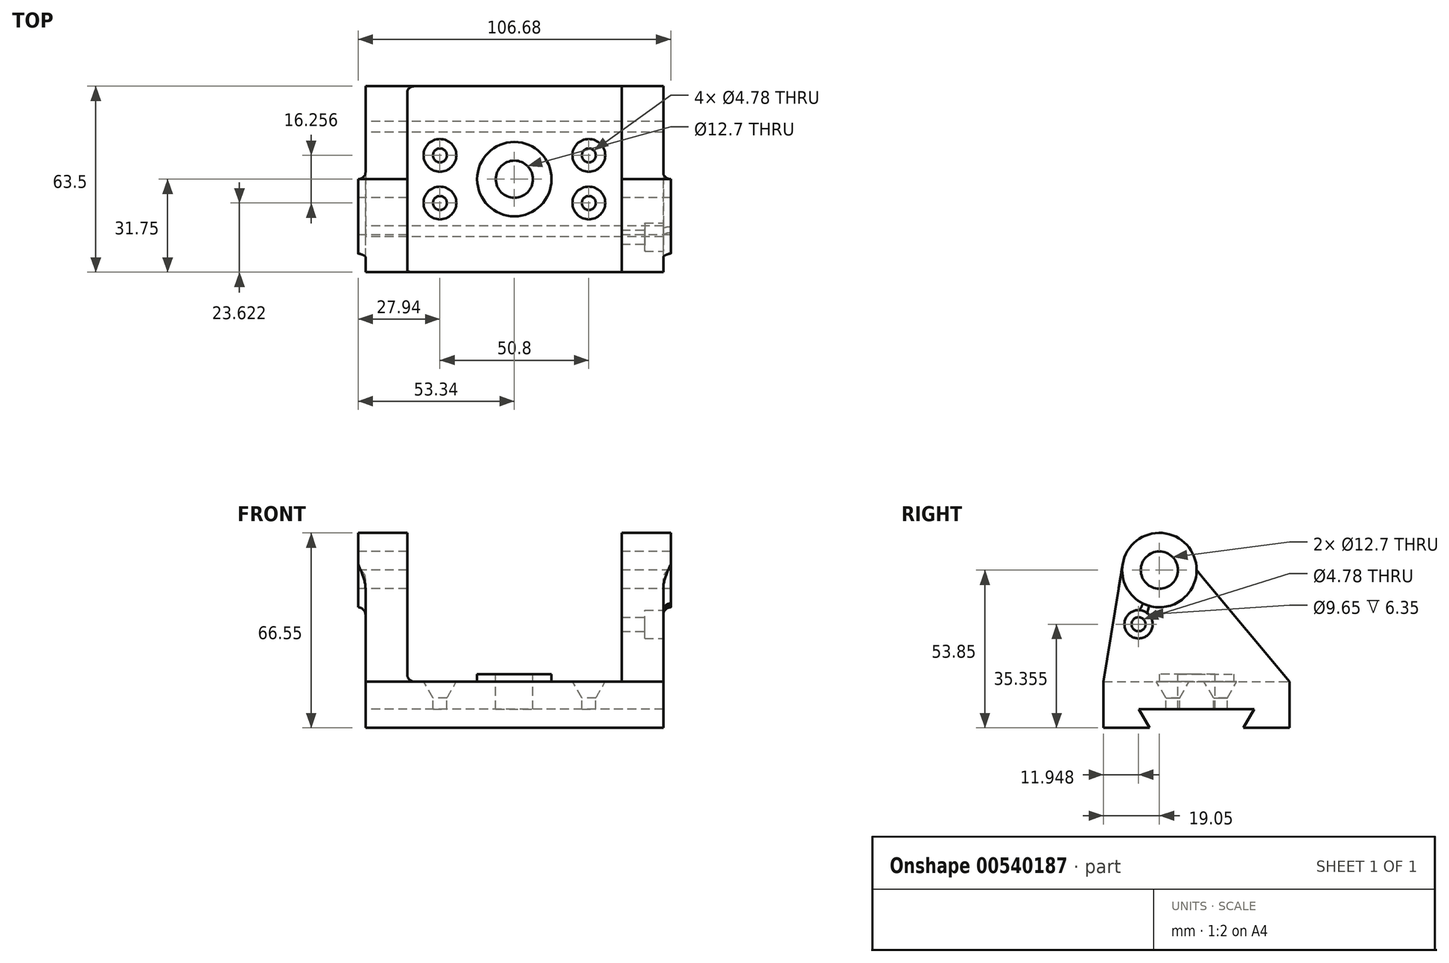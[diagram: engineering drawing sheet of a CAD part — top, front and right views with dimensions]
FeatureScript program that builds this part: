
annotation { "Feature Type Name" : "Feature", "Feature Type Description" : "" }
export const myFeature = defineFeature(function(context is Context, id is Id, definition is map)
    precondition{}
    {
        {
            var Q0;
            Q0=qCreatedBy(makeId("Right.planeOp"),FACE);
            var sketch = newSketch(context, id + "F0", { "sketchPlane" : qUnion([Q0])});
            skLineSegment(sketch, "E0", {"start": v(0, -77.1) * mm, "end": v(0, 79.46) * mm, "construction": true});
            skLineSegment(sketch, "E1", {"start": v(-83.92, 0) * mm, "end": v(89.2, 0) * mm, "construction": true});
            skLineSegment(sketch, "E2", {"start": v(-31.75, 0) * mm, "end": v(-31.75, -15.75) * mm});
            skLineSegment(sketch, "E3", {"start": v(-31.75, -15.75) * mm, "end": v(-16, -15.75) * mm});
            skCircle(sketch, "E4", {"center": v(-12.7, 38.1) * mm, "radius": 12.7 * mm});
            skCircle(sketch, "E5", {"center": v(-12.7, 38.1) * mm, "radius": 6.35 * mm});
            skLineSegment(sketch, "E6", {"start": v(-31.75, 0) * mm, "end": v(-25.24, 40.13) * mm});
            skLineSegment(sketch, "E7", {"start": v(0, -9.4) * mm, "end": v(-19.67, -9.4) * mm});
            skLineSegment(sketch, "E8", {"start": v(-19.67, -9.4) * mm, "end": v(-16, -15.75) * mm});
            skLineSegment(sketch, "E9.MirrorCS", {"start": v(0, -9.4) * mm, "end": v(19.67, -9.4) * mm});
            skLineSegment(sketch, "E10.MirrorCS", {"start": v(19.67, -9.4) * mm, "end": v(16, -15.75) * mm});
            skLineSegment(sketch, "E11.MirrorCS", {"start": v(31.75, -15.75) * mm, "end": v(16, -15.75) * mm});
            skLineSegment(sketch, "E12.MirrorCS", {"start": v(31.75, 0) * mm, "end": v(31.75, -15.75) * mm});
            skLineSegment(sketch, "E13", {"start": v(31.75, 0) * mm, "end": v(0, 38.1) * mm});
            skLineSegment(sketch, "E14", {"start": v(-31.75, 0) * mm, "end": v(31.75, 0) * mm});
            skSolve(sketch);
        }
        {
            var Q0;
            Q0=makeQuery(id+"F0.imprint","IMPRINT",FACE,{"disambiguationData":[TD([[makeQuery(id+"F0.imprint","IMPRINT",EDGE,{"derivedFrom":sQuery(id+"F0.wireOp",EDGE,"E2")}),1.0]])]});
            var Q1;
            Q1=makeQuery(id+"F0.imprint","IMPRINT",FACE,{"disambiguationData":[TD([[makeQuery(id+"F0.imprint","IMPRINT",EDGE,{"derivedFrom":sQuery(id+"F0.wireOp",EDGE,"E5")}),-1.0]])]});
            var Q2;
            {var subQ0=sQuery(id+"F0.wireOp",EDGE,"E6");Q2=makeQuery(id+"F0.imprint","IMPRINT",FACE,{"disambiguationData":[TD([[makeQuery(id+"F0.imprint","IMPRINT",EDGE,{"derivedFrom":subQ0}),-1.0]])]});}
            extrude(context, id + "F1", {"entities" : qUnion([Q0, Q1, Q2]), "endBound" : BoundingType.SYMMETRIC, "depth" : 101.6 * mm, "offsetDistance" : 25.4 * mm});
        }
        {
            var Q0;
            Q0=makeQuery(id+"F0.imprint","IMPRINT",FACE,{"disambiguationData":[TD([[makeQuery(id+"F0.imprint","IMPRINT",EDGE,{"derivedFrom":sQuery(id+"F0.wireOp",EDGE,"E5")}),-1.0]])]});
            extrude(context, id + "F2", {"entities" : qUnion([Q0]), "operationType" : NewBodyOperationType.ADD, "endBound" : BoundingType.SYMMETRIC, "depth" : 106.68 * mm, "offsetDistance" : 25.4 * mm});
        }
        {
            var Q0;
            {var subQ0=sQuery(id+"F0.wireOp",EDGE,"E6");Q0=makeQuery(id+"F0.imprint","IMPRINT",FACE,{"disambiguationData":[TD([[makeQuery(id+"F0.imprint","IMPRINT",EDGE,{"derivedFrom":subQ0}),-1.0]])]});}
            var Q1;
            Q1=makeQuery(id+"F0.imprint","IMPRINT",FACE,{"disambiguationData":[TD([[makeQuery(id+"F0.imprint","IMPRINT",EDGE,{"derivedFrom":sQuery(id+"F0.wireOp",EDGE,"E5")}),-1.0]])]});
            extrude(context, id + "F3", {"entities" : qUnion([Q0, Q1]), "operationType" : NewBodyOperationType.REMOVE, "endBound" : BoundingType.SYMMETRIC, "oppositeDirection" : true, "depth" : 73.15 * mm, "offsetDistance" : 25.4 * mm});
        }
        {
            var Q0;
            Q0=makeQuery(id+"F3.boolean.opBoolean","COPY",FACE,{"derivedFrom":makeQuery(id+"F3.opExtrude","SWEPT_FACE",FACE,{"disambiguationData":[OSD([sQuery(id+"F0.wireOp",EDGE,"E14")])]})});
            var sketch = newSketch(context, id + "F4", { "sketchPlane" : qUnion([Q0])});
            skPoint(sketch, "E15", {"position": v(-25.4, 8.13) * mm});
            skPoint(sketch, "E16", {"position": v(25.4, 8.13) * mm});
            skPoint(sketch, "E17", {"position": v(25.4, -8.13) * mm});
            skPoint(sketch, "E18", {"position": v(-25.4, -8.13) * mm});
            skCircle(sketch, "E19", {"center": v(0, 0) * mm, "radius": 12.7 * mm});
            skCircle(sketch, "E20", {"center": v(0, 0) * mm, "radius": 6.35 * mm});
            skSolve(sketch);
        }
        {
            var Q0;
            Q0=sQuery(id+"F4.wireOp",VERTEX,"E15");
            var Q1;
            Q1=sQuery(id+"F4.wireOp",VERTEX,"E18");
            var Q2;
            Q2=sQuery(id+"F4.wireOp",VERTEX,"E16");
            var Q3;
            Q3=sQuery(id+"F4.wireOp",VERTEX,"E17");
            var Q4;
            Q4=makeQuery(id+"F1.opExtrude","SWEPT_BODY",BODY,{"disambiguationData":[OSD([sQuery(id+"F0.wireOp",EDGE,"E2"),sQuery(id+"F0.wireOp",EDGE,"E3"),sQuery(id+"F0.wireOp",EDGE,"E4"),sQuery(id+"F0.wireOp",EDGE,"E5"),sQuery(id+"F0.wireOp",EDGE,"E6"),sQuery(id+"F0.wireOp",EDGE,"E7"),sQuery(id+"F0.wireOp",EDGE,"E8"),sQuery(id+"F0.wireOp",EDGE,"E9.MirrorCS"),sQuery(id+"F0.wireOp",EDGE,"E10.MirrorCS"),sQuery(id+"F0.wireOp",EDGE,"E11.MirrorCS"),sQuery(id+"F0.wireOp",EDGE,"E12.MirrorCS"),sQuery(id+"F0.wireOp",EDGE,"E13")])]});
            hole(context, id + "F5", {"style" : HoleStyle.C_SINK, "endStyle" : HoleEndStyle.THROUGH, "holeDiameter" : 4.78 * mm, "cSinkDiameter" : 11.18 * mm, "cSinkAngle" : 60 * degree, "isTappedThrough" : true, "tappedDepth" : 12.7 * mm, "tapClearance" : 3, "locations" : qUnion([Q0, Q1, Q2, Q3]), "scope" : qUnion([Q4])});
        }
        {
            var Q0;
            Q0=makeQuery(id+"F4.imprint","IMPRINT",FACE,{"disambiguationData":[TD([[makeQuery(id+"F4.imprint","IMPRINT",EDGE,{"derivedFrom":sQuery(id+"F4.wireOp",EDGE,"E20")}),1.0]])]});
            extrude(context, id + "F6", {"entities" : qUnion([Q0]), "operationType" : NewBodyOperationType.REMOVE, "endBound" : BoundingType.UP_TO_NEXT, "oppositeDirection" : true, "depth" : 25.4 * mm, "offsetDistance" : 25.4 * mm});
        }
        {
            var Q0;
            Q0=makeQuery(id+"F4.imprint","IMPRINT",FACE,{"disambiguationData":[TD([[makeQuery(id+"F4.imprint","IMPRINT",EDGE,{"derivedFrom":sQuery(id+"F4.wireOp",EDGE,"E19")}),1.0]])]});
            extrude(context, id + "F7", {"entities" : qUnion([Q0]), "operationType" : NewBodyOperationType.ADD, "depth" : 2.54 * mm, "offsetDistance" : 25.4 * mm});
        }
        {
            var Q0;
            Q0=makeQuery(id+"F1.opExtrude","CAP_FACE",FACE,{"disambiguationData":[OSD([sQuery(id+"F0.wireOp",EDGE,"E2"),sQuery(id+"F0.wireOp",EDGE,"E3"),sQuery(id+"F0.wireOp",EDGE,"E4"),sQuery(id+"F0.wireOp",EDGE,"E5"),sQuery(id+"F0.wireOp",EDGE,"E6"),sQuery(id+"F0.wireOp",EDGE,"E7"),sQuery(id+"F0.wireOp",EDGE,"E8"),sQuery(id+"F0.wireOp",EDGE,"E9.MirrorCS"),sQuery(id+"F0.wireOp",EDGE,"E10.MirrorCS"),sQuery(id+"F0.wireOp",EDGE,"E11.MirrorCS"),sQuery(id+"F0.wireOp",EDGE,"E12.MirrorCS"),sQuery(id+"F0.wireOp",EDGE,"E13")])],"isStart":false});
            var sketch = newSketch(context, id + "F8", { "sketchPlane" : qUnion([Q0])});
            skPoint(sketch, "E21", {"position": v(-19.8, 19.6) * mm});
            skSolve(sketch);
        }
        {
            var Q0;
            Q0=sQuery(id+"F8.wireOp",VERTEX,"E21");
            var Q1;
            Q1=makeQuery(id+"F1.opExtrude","SWEPT_BODY",BODY,{"disambiguationData":[OSD([sQuery(id+"F0.wireOp",EDGE,"E2"),sQuery(id+"F0.wireOp",EDGE,"E3"),sQuery(id+"F0.wireOp",EDGE,"E4"),sQuery(id+"F0.wireOp",EDGE,"E5"),sQuery(id+"F0.wireOp",EDGE,"E6"),sQuery(id+"F0.wireOp",EDGE,"E7"),sQuery(id+"F0.wireOp",EDGE,"E8"),sQuery(id+"F0.wireOp",EDGE,"E9.MirrorCS"),sQuery(id+"F0.wireOp",EDGE,"E10.MirrorCS"),sQuery(id+"F0.wireOp",EDGE,"E11.MirrorCS"),sQuery(id+"F0.wireOp",EDGE,"E12.MirrorCS"),sQuery(id+"F0.wireOp",EDGE,"E13")])]});
            hole(context, id + "F9", {"style" : HoleStyle.C_BORE, "endStyle" : HoleEndStyle.BLIND, "holeDiameter" : 4.78 * mm, "cBoreDiameter" : 9.65 * mm, "cBoreDepth" : 6.35 * mm, "holeDepth" : 17.78 * mm, "isTappedThrough" : true, "tappedDepth" : 12.7 * mm, "tapClearance" : 3, "startFromSketch" : true, "locations" : qUnion([Q0]), "scope" : qUnion([Q1])});
        }
        {
            var Q0;
            Q0=makeQuery(id+"F3.boolean.opBoolean","COPY",EDGE,{"derivedFrom":makeQuery(id+"F3.opExtrude","CAP_EDGE",EDGE,{"disambiguationData":[OSD([sQuery(id+"F0.wireOp",EDGE,"E14")])],"isStart":false})});
            var Q1;
            Q1=makeQuery(id+"F7.opExtrude","CAP_EDGE",EDGE,{"disambiguationData":[OSD([sQuery(id+"F4.wireOp",EDGE,"E19")])],"isStart":true});
            var Q2;
            {var subQ0=sQuery(id+"F0.wireOp",EDGE,"E4");Q2=makeQuery(id+"F2.boolean.opBoolean","INTERSECT",EDGE,{"derivedFrom":[makeQuery(id+"F1.opExtrude","CAP_FACE",FACE,{"disambiguationData":[OSD([sQuery(id+"F0.wireOp",EDGE,"E2"),sQuery(id+"F0.wireOp",EDGE,"E3"),subQ0,sQuery(id+"F0.wireOp",EDGE,"E5"),sQuery(id+"F0.wireOp",EDGE,"E6"),sQuery(id+"F0.wireOp",EDGE,"E7"),sQuery(id+"F0.wireOp",EDGE,"E8"),sQuery(id+"F0.wireOp",EDGE,"E9.MirrorCS"),sQuery(id+"F0.wireOp",EDGE,"E10.MirrorCS"),sQuery(id+"F0.wireOp",EDGE,"E11.MirrorCS"),sQuery(id+"F0.wireOp",EDGE,"E12.MirrorCS"),sQuery(id+"F0.wireOp",EDGE,"E13")])],"isStart":false}),makeQuery(id+"F2.opExtrude","SWEPT_FACE",FACE,{"disambiguationData":[OSD([subQ0])]})]});}
            var Q3;
            {var subQ0=sQuery(id+"F0.wireOp",EDGE,"E4");Q3=makeQuery(id+"F2.boolean.opBoolean","INTERSECT",EDGE,{"derivedFrom":[makeQuery(id+"F1.opExtrude","CAP_FACE",FACE,{"disambiguationData":[OSD([sQuery(id+"F0.wireOp",EDGE,"E2"),sQuery(id+"F0.wireOp",EDGE,"E3"),subQ0,sQuery(id+"F0.wireOp",EDGE,"E5"),sQuery(id+"F0.wireOp",EDGE,"E6"),sQuery(id+"F0.wireOp",EDGE,"E7"),sQuery(id+"F0.wireOp",EDGE,"E8"),sQuery(id+"F0.wireOp",EDGE,"E9.MirrorCS"),sQuery(id+"F0.wireOp",EDGE,"E10.MirrorCS"),sQuery(id+"F0.wireOp",EDGE,"E11.MirrorCS"),sQuery(id+"F0.wireOp",EDGE,"E12.MirrorCS"),sQuery(id+"F0.wireOp",EDGE,"E13")])],"isStart":true}),makeQuery(id+"F2.opExtrude","SWEPT_FACE",FACE,{"disambiguationData":[OSD([subQ0])]})]});}
            fillet(context, id + "F10", {"entities" : qUnion([Q0, Q1, Q2, Q3]), "radius" : 2.54 * mm, "tangentPropagation" : true, "allowEdgeOverflow" : false});
        }
    });
